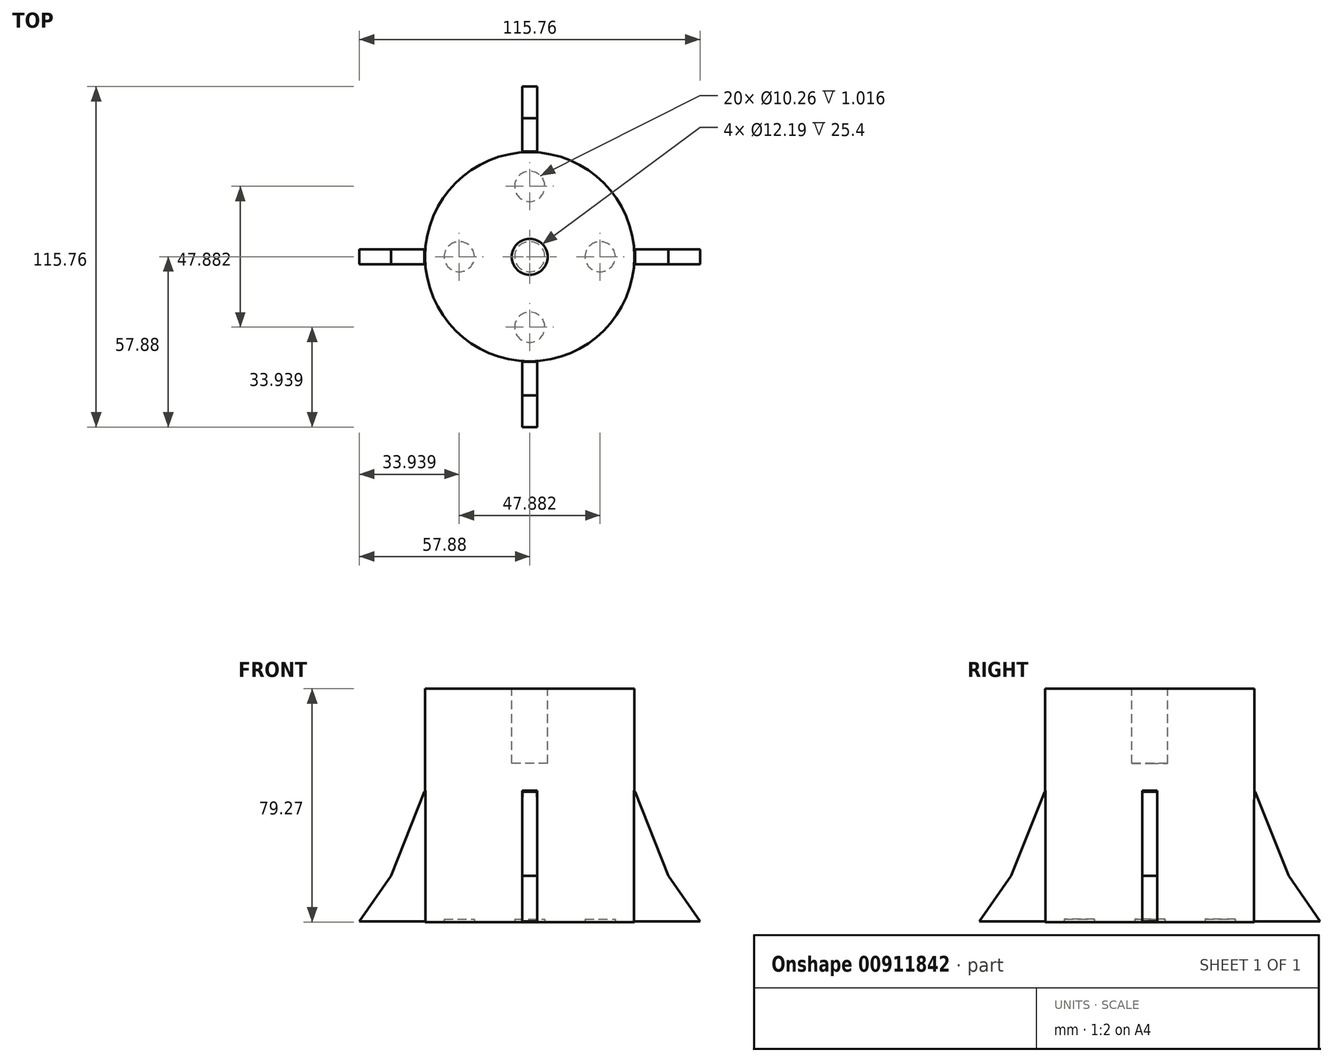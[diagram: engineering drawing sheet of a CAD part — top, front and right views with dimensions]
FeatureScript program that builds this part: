
annotation { "Feature Type Name" : "Feature", "Feature Type Description" : "" }
export const myFeature = defineFeature(function(context is Context, id is Id, definition is map)
    precondition{}
    {
        {
            var Q0;
            Q0=qCreatedBy(makeId("Front.planeOp"),FACE);
            var sketch = newSketch(context, id + "F0", { "sketchPlane" : qUnion([Q0])});
            skLineSegment(sketch, "E0.bottom", {"start": v(0, -79.27) * mm, "end": v(-35.56, -79.27) * mm});
            skLineSegment(sketch, "E0.top", {"start": v(0, 0) * mm, "end": v(-35.56, 0) * mm});
            skLineSegment(sketch, "E0.left", {"start": v(0, -79.27) * mm, "end": v(0, 0) * mm});
            skLineSegment(sketch, "E0.right", {"start": v(-35.56, -79.27) * mm, "end": v(-35.56, 0) * mm});
            skLineSegment(sketch, "E1", {"start": v(0, 6.53) * mm, "end": v(0, -84.12) * mm});
            skLineSegment(sketch, "E2", {"start": v(-35.56, -19.86) * mm, "end": v(0, -19.86) * mm});
            skLineSegment(sketch, "E3", {"start": v(-33.06, -19.86) * mm, "end": v(-33.06, 0) * mm});
            skLineSegment(sketch, "E4", {"start": v(-30.99, 0) * mm, "end": v(-30.99, -19.86) * mm});
            skLineSegment(sketch, "E5", {"start": v(-30.99, -19.86) * mm, "end": v(-28.92, -19.86) * mm});
            skLineSegment(sketch, "E6", {"start": v(-28.92, -19.86) * mm, "end": v(-28.92, 0) * mm});
            skLineSegment(sketch, "E7", {"start": v(-28.92, 0) * mm, "end": v(-26.01, 0) * mm});
            skLineSegment(sketch, "E8", {"start": v(-26.01, 0) * mm, "end": v(-26.01, -19.86) * mm});
            skLineSegment(sketch, "E9", {"start": v(-26.01, -19.86) * mm, "end": v(-23.73, -19.86) * mm});
            skLineSegment(sketch, "E10", {"start": v(-23.73, -19.86) * mm, "end": v(-23.73, 0) * mm});
            skLineSegment(sketch, "E11", {"start": v(-23.73, 0) * mm, "end": v(-21.45, 0) * mm});
            skLineSegment(sketch, "E12", {"start": v(-21.45, 0) * mm, "end": v(-21.45, -19.86) * mm});
            skLineSegment(sketch, "E13", {"start": v(-21.45, -19.86) * mm, "end": v(-17.78, -19.86) * mm});
            skLineSegment(sketch, "E14", {"start": v(-17.78, -19.86) * mm, "end": v(-17.78, 0) * mm});
            skLineSegment(sketch, "E15", {"start": v(-17.78, 0) * mm, "end": v(-19.8, 0) * mm});
            skLineSegment(sketch, "E16", {"start": v(-19.8, 0) * mm, "end": v(-19.8, -19.86) * mm});
            skLineSegment(sketch, "E17", {"start": v(-19.8, -19.86) * mm, "end": v(-15.24, -19.86) * mm});
            skLineSegment(sketch, "E18", {"start": v(-15.24, -19.86) * mm, "end": v(-15.24, 0) * mm});
            skLineSegment(sketch, "E19", {"start": v(-15.24, 0) * mm, "end": v(-12.33, 0) * mm});
            skLineSegment(sketch, "E20", {"start": v(-12.33, 0) * mm, "end": v(-12.33, -19.86) * mm});
            skLineSegment(sketch, "E21", {"start": v(-12.33, -19.86) * mm, "end": v(-9.85, -19.86) * mm});
            skLineSegment(sketch, "E22", {"start": v(-9.85, -19.86) * mm, "end": v(-9.85, 0) * mm});
            skLineSegment(sketch, "E23", {"start": v(-9.85, 0) * mm, "end": v(-7.36, 0) * mm});
            skLineSegment(sketch, "E24", {"start": v(-7.36, 0) * mm, "end": v(-7.36, -19.86) * mm});
            skLineSegment(sketch, "E25", {"start": v(-7.36, -19.86) * mm, "end": v(-5.29, -19.86) * mm});
            skLineSegment(sketch, "E26", {"start": v(-5.29, -19.86) * mm, "end": v(-5.29, 0) * mm});
            skLineSegment(sketch, "E27", {"start": v(-3.42, 0) * mm, "end": v(-3.42, -19.86) * mm});
            skLineSegment(sketch, "E28", {"start": v(-3.42, -19.86) * mm, "end": v(0, -19.86) * mm});
            skSolve(sketch);
        }
        {
            var Q0;
            Q0 = qSketchRegion(id + "F0", true);
            var Q1;
            Q1=sQuery(id+"F0.wireOp",EDGE,"E1");
            revolve(context, id + "F1", {"surfaceOperationType" : NewSurfaceOperationType.NEW, "entities" : qUnion([Q0]), "axis" : qUnion([Q1]), "revolveType" : RevolveType.FULL});
        }
        {
            var Q0;
            Q0=qCreatedBy(makeId("Front.planeOp"),FACE);
            var sketch = newSketch(context, id + "F2", { "sketchPlane" : qUnion([Q0])});
            skLineSegment(sketch, "E29", {"start": v(35.13, -79.1) * mm, "end": v(47.16, -79.1) * mm});
            skLineSegment(sketch, "E30", {"start": v(47.16, -79.1) * mm, "end": v(47.16, -63.55) * mm});
            skLineSegment(sketch, "E31", {"start": v(47.16, -63.55) * mm, "end": v(35.76, -34.95) * mm});
            skLineSegment(sketch, "E32", {"start": v(57.88, -79.1) * mm, "end": v(47.16, -63.55) * mm});
            skLineSegment(sketch, "E33", {"start": v(35.76, -34.95) * mm, "end": v(35.48, -34.56) * mm});
            skLineSegment(sketch, "E34", {"start": v(35.57, 0) * mm, "end": v(35.48, -36.67) * mm});
            skLineSegment(sketch, "E35", {"start": v(35.48, -36.67) * mm, "end": v(35.13, -79.1) * mm});
            skLineSegment(sketch, "E36", {"start": v(47.16, -79.1) * mm, "end": v(57.88, -79.1) * mm});
            skSolve(sketch);
        }
        {
            var Q0;
            Q0=makeQuery(id+"F2.imprint","IMPRINT",FACE,{"disambiguationData":[TD([[makeQuery(id+"F2.imprint","IMPRINT",EDGE,{"derivedFrom":sQuery(id+"F2.wireOp",EDGE,"E29")}),1.0]])]});
            var Q1;
            Q1=makeQuery(id+"F2.imprint","IMPRINT",FACE,{"disambiguationData":[TD([[makeQuery(id+"F2.imprint","IMPRINT",EDGE,{"derivedFrom":sQuery(id+"F2.wireOp",EDGE,"E30")}),-1.0]])]});
            extrude(context, id + "F3", {"entities" : qUnion([Q0, Q1]), "operationType" : NewBodyOperationType.ADD, "endBound" : BoundingType.SYMMETRIC, "depth" : 5.08 * mm, "offsetDistance" : 25.4 * mm});
        }
        {
            var Q0;
            Q0=makeQuery(id+"F1.opRevolve","SWEPT_BODY",BODY,{"disambiguationData":[OSD([sQuery(id+"F0.wireOp",EDGE,"E0.bottom"),sQuery(id+"F0.wireOp",EDGE,"E0.top"),sQuery(id+"F0.wireOp",EDGE,"E0.right"),sQuery(id+"F0.wireOp",EDGE,"E1"),sQuery(id+"F0.wireOp",EDGE,"E7"),sQuery(id+"F0.wireOp",EDGE,"E11"),sQuery(id+"F0.wireOp",EDGE,"E15"),sQuery(id+"F0.wireOp",EDGE,"E19"),sQuery(id+"F0.wireOp",EDGE,"E23")])]});
            var Q1;
            Q1=sQuery(id+"F0.wireOp",EDGE,"E1");
            circularPattern(context, id + "F4", {"entities" : qUnion([Q0]), "axis" : qUnion([Q1]), "angle" : 360 * degree, "instanceCount" : 4, "equalSpace" : true});
        }
        {
            var Q0;
            Q0=makeQuery(id+"F1.opRevolve","SWEPT_FACE",FACE,{"disambiguationData":[OSD([sQuery(id+"F0.wireOp",EDGE,"E0.bottom")])]});
            var sketch = newSketch(context, id + "F5", { "sketchPlane" : qUnion([Q0])});
            skCircle(sketch, "E37", {"center": v(0, 0) * mm, "radius": 5.13 * mm});
            skCircle(sketch, "E38", {"center": v(-23.94, 0) * mm, "radius": 5.13 * mm});
            skCircle(sketch, "E39.1.0", {"center": v(0, 23.94) * mm, "radius": 5.13 * mm});
            skCircle(sketch, "E39.2.0", {"center": v(23.94, 0) * mm, "radius": 5.13 * mm});
            skCircle(sketch, "E39.3.0", {"center": v(0, -23.94) * mm, "radius": 5.13 * mm});
            skLineSegment(sketch, "E39.anchor1", {"start": v(0, 0) * mm, "end": v(-23.94, 0) * mm, "construction": true});
            skLineSegment(sketch, "E39.anchor2", {"start": v(0, 0) * mm, "end": v(0, -23.94) * mm, "construction": true});
            skSolve(sketch);
        }
        {
            var Q0;
            Q0 = qSketchRegion(id + "F5", true);
            extrude(context, id + "F6", {"entities" : qUnion([Q0]), "operationType" : NewBodyOperationType.REMOVE, "oppositeDirection" : true, "depth" : 1.02 * mm, "offsetDistance" : 25.4 * mm});
        }
        {
            var Q0;
            Q0=qCreatedBy(makeId("Top.planeOp"),FACE);
            var sketch = newSketch(context, id + "F7", { "sketchPlane" : qUnion([Q0])});
            skCircle(sketch, "E40", {"center": v(0, 0) * mm, "radius": 6.1 * mm});
            skSolve(sketch);
        }
        {
            var Q0;
            Q0 = qSketchRegion(id + "F7", true);
            extrude(context, id + "F8", {"entities" : qUnion([Q0]), "operationType" : NewBodyOperationType.REMOVE, "oppositeDirection" : true, "depth" : 25.4 * mm, "offsetDistance" : 25.4 * mm});
        }
    });
